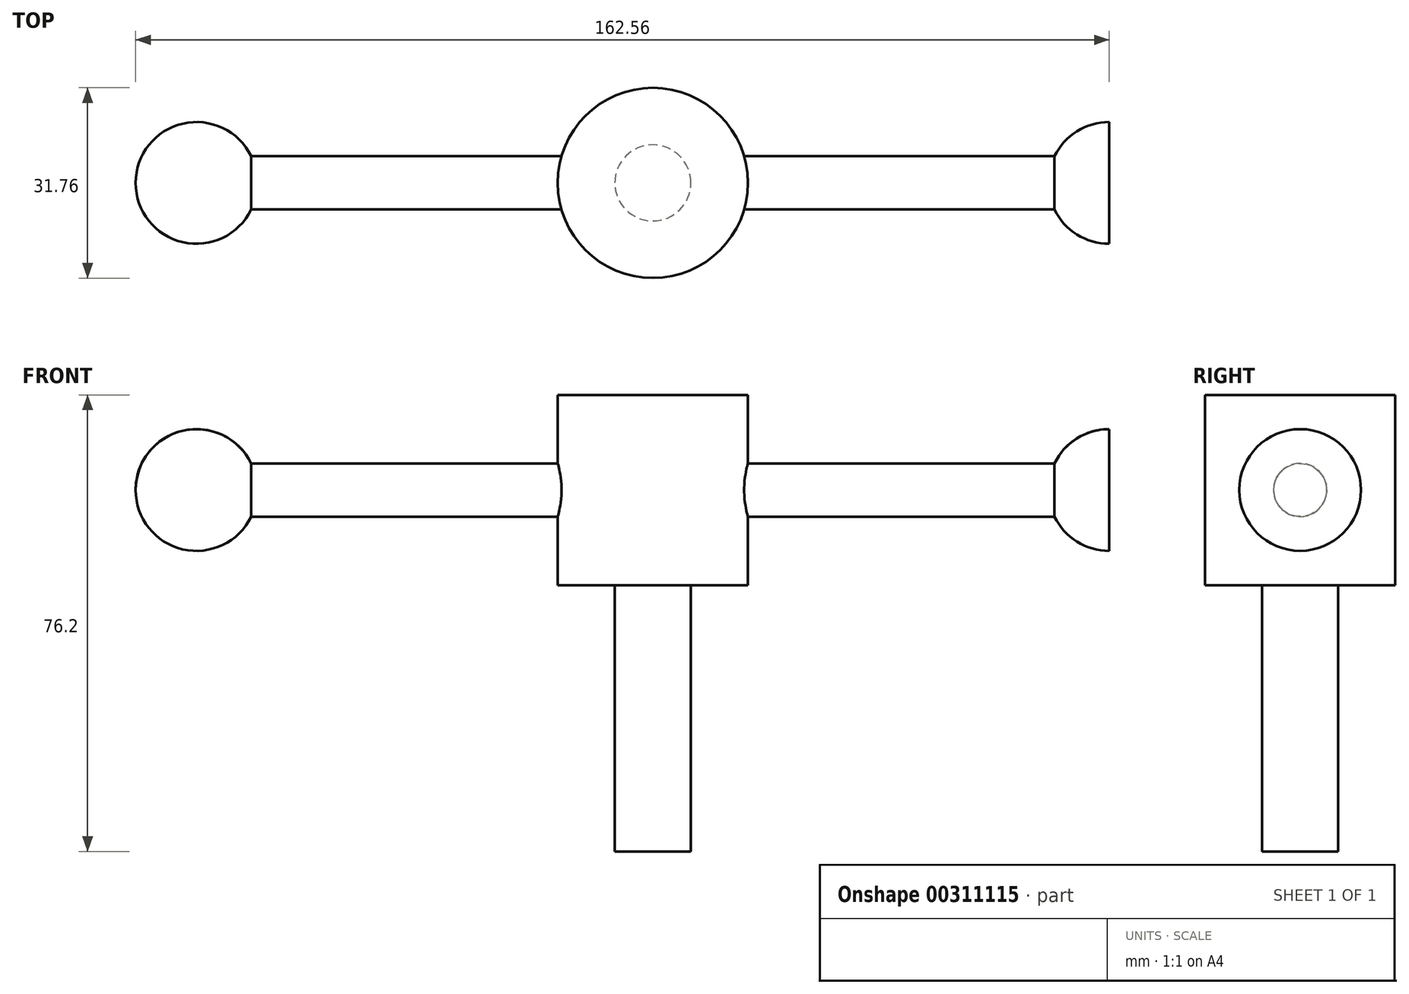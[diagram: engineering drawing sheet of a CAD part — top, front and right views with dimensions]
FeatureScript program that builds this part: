
annotation { "Feature Type Name" : "Feature", "Feature Type Description" : "" }
export const myFeature = defineFeature(function(context is Context, id is Id, definition is map)
    precondition{}
    {
        {
            var Q0;
            Q0=qCreatedBy(makeId("Top.planeOp"),FACE);
            var sketch = newSketch(context, id + "F0", { "sketchPlane" : qUnion([Q0])});
            skCircle(sketch, "E0", {"center": v(0, 0) * mm, "radius": 15.88 * mm});
            skSolve(sketch);
        }
        {
            var Q0;
            Q0 = qSketchRegion(id + "F0", true);
            extrude(context, id + "F1", {"entities" : qUnion([Q0]), "depth" : 31.75 * mm});
        }
        {
            var Q0;
            Q0=makeQuery(id+"F1.opExtrude","CAP_FACE",FACE,{"disambiguationData":[OSD([sQuery(id+"F0.wireOp",EDGE,"E0")])],"isStart":true});
            var sketch = newSketch(context, id + "F2", { "sketchPlane" : qUnion([Q0])});
            skCircle(sketch, "E1", {"center": v(0, 0) * mm, "radius": 6.35 * mm});
            skSolve(sketch);
        }
        {
            var Q0;
            Q0 = qSketchRegion(id + "F2", true);
            extrude(context, id + "F3", {"entities" : qUnion([Q0]), "operationType" : NewBodyOperationType.ADD, "depth" : 44.45 * mm});
        }
        {
            var Q0;
            Q0=qCreatedBy(makeId("Right.planeOp"),FACE);
            var sketch = newSketch(context, id + "F4", { "sketchPlane" : qUnion([Q0])});
            skLineSegment(sketch, "E2", {"start": v(0, 0) * mm, "end": v(0, 31.75) * mm, "construction": true});
            skCircle(sketch, "E3", {"center": v(0, 15.88) * mm, "radius": 4.45 * mm});
            skSolve(sketch);
        }
        {
            var Q0;
            Q0 = qSketchRegion(id + "F4", true);
            extrude(context, id + "F5", {"entities" : qUnion([Q0]), "operationType" : NewBodyOperationType.ADD, "endBound" : BoundingType.SYMMETRIC, "depth" : 152.4 * mm});
        }
        {
            var Q0;
            Q0=qCreatedBy(makeId("Front.planeOp"),FACE);
            var sketch = newSketch(context, id + "F6", { "sketchPlane" : qUnion([Q0])});
            skLineSegment(sketch, "E4", {"start": v(-76.2, 20.32) * mm, "end": v(-15.87, 20.32) * mm});
            skLineSegment(sketch, "E5", {"start": v(-15.87, 11.43) * mm, "end": v(-76.2, 11.43) * mm});
            skLineSegment(sketch, "E6", {"start": v(15.88, 20.32) * mm, "end": v(76.2, 20.32) * mm});
            skLineSegment(sketch, "E7", {"start": v(76.2, 11.43) * mm, "end": v(15.88, 11.43) * mm});
            skLineSegment(sketch, "E8", {"start": v(-76.2, 20.32) * mm, "end": v(-76.2, 11.43) * mm, "construction": true});
            skArc(sketch, "E9", {"start": v(-67.06, 11.43) * mm, "mid": v(-73.92, 25.78) * mm, "end": v(-86.36, 15.88) * mm});
            skLineSegment(sketch, "E10", {"start": v(76.2, 20.32) * mm, "end": v(76.2, 11.43) * mm, "construction": true});
            skArc(sketch, "E11", {"start": v(86.36, 15.88) * mm, "mid": v(73.92, 25.78) * mm, "end": v(67.06, 11.43) * mm});
            skLineSegment(sketch, "E12", {"start": v(-76.2, 15.88) * mm, "end": v(-76.2, 26.04) * mm, "construction": true});
            skLineSegment(sketch, "E13", {"start": v(-76.2, 26.04) * mm, "end": v(-76.2, 5.71) * mm, "construction": true});
            skLineSegment(sketch, "E14", {"start": v(76.2, 15.88) * mm, "end": v(76.2, 26.04) * mm, "construction": true});
            skLineSegment(sketch, "E15", {"start": v(76.2, 26.04) * mm, "end": v(76.2, 11.43) * mm, "construction": true});
            skLineSegment(sketch, "E16", {"start": v(-76.2, 15.88) * mm, "end": v(-86.36, 15.88) * mm, "construction": true});
            skLineSegment(sketch, "E17", {"start": v(-86.36, 15.88) * mm, "end": v(-76.2, 15.88) * mm});
            skLineSegment(sketch, "E18", {"start": v(-76.2, 15.88) * mm, "end": v(-76.2, 20.32) * mm});
            skLineSegment(sketch, "E19", {"start": v(76.2, 15.88) * mm, "end": v(86.36, 15.88) * mm});
            skLineSegment(sketch, "E20", {"start": v(86.36, 15.88) * mm, "end": v(76.2, 15.88) * mm});
            skLineSegment(sketch, "E21", {"start": v(76.2, 11.43) * mm, "end": v(67.06, 11.43) * mm});
            skLineSegment(sketch, "E22", {"start": v(76.2, 20.32) * mm, "end": v(76.2, 5.05) * mm, "construction": true});
            skLineSegment(sketch, "E23", {"start": v(76.2, 15.88) * mm, "end": v(76.2, 26.04) * mm});
            skSolve(sketch);
        }
        {
            var Q0;
            {var subQ4=sQuery(id+"F6.wireOp",EDGE,"E17");Q0=makeQuery(id+"F6.imprint","IMPRINT",FACE,{"disambiguationData":[TD([[makeQuery(id+"F6.imprint","IMPRINT",EDGE,{"derivedFrom":subQ4}),1.0]])]});}
            var Q1;
            {var subQ0=sQuery(id+"F6.wireOp",EDGE,"E20");Q1=makeQuery(id+"F6.imprint","IMPRINT",FACE,{"disambiguationData":[TD([[makeQuery(id+"F6.imprint","IMPRINT",EDGE,{"derivedFrom":subQ0}),-1.0]])]});}
            var Q2;
            {var subQ0=sQuery(id+"F6.wireOp",EDGE,"E23");var subQ1=sQuery(id+"F6.wireOp",EDGE,"E6");var subQ2=makeQuery(id+"F6.imprint","INTERSECT",VERTEX,{"derivedFrom":[subQ1,subQ0]});Q2=makeQuery(id+"F6.imprint","IMPRINT",FACE,{"disambiguationData":[TD([[makeQuery(id+"F6.imprint","IMPRINT",EDGE,{"disambiguationData":[TD([[subQ2,1.0]])],"derivedFrom":subQ1}),1.0]])]});}
            var Q3;
            Q3=sQuery(id+"F6.wireOp",EDGE,"E17");
            revolve(context, id + "F7", {"operationType" : NewBodyOperationType.ADD, "entities" : qUnion([Q0, Q1, Q2]), "axis" : qUnion([Q3]), "revolveType" : RevolveType.FULL});
        }
    });
